# Revit family: HVAC-Fireplaces_Kalfire Fireplaces_e-one-130s-holographic-fireplace1
name_source: partatom
category: Specialty Equipment
units: mm (PartAtom-declared; Revit-internal decimal feet)

## family parameters
Cut with Voids When Loaded = No
Host = Face
OmniClass Number = 23.19.17.00
OmniClass Title = Fireplaces
Part Type = Normal
Room Calculation Point = No
Round Connector Dimension = Use Diameter
Shared = No

## types (1)
- E-one 130S Holographic Fireplace
    Area required = 1000 mm²
    Assembly Code = D3020.10
    Consumption (excl. Atmos Heating) = 110 W
    Consumption (incl. Atmos Heating) = 2 kW
    Date Updated = -
    Default Elevation = 1219 mm
    Description = The Kalfire E-one 130S is an electric holographic fireplace with glass on the front, both sides and optional heating. The projection of 3D holographic flames on the handmade logs imitates true-to-life fire. Options such as the realistic glow bed, crackling sound and optional Atmos Heating ensure an optimal fire experience.

A three-sided model is suitable as a see-through fireplace and takes your interior to the next level. Admire the holographic flames through the sides and be amazed by the realistic fire. At 130 cm wide, the E-one 130S is also perfectly used as a cinewall. Kalfire E-one holographic ambient fireplaces can be customised to suit personal preferences. Our exclusive and certified dealers are your helping hand in the installation and realisation of your dream design.

Atmos Heating: atmosphere fire with heat

The E-one is available with an innovative heating element called Atmos Heating. This element is exclusively available for the built-in versions of the Kalfire E-one (all variants except the E-one 100F FR). The heating element provides a pleasant and continuous flow of warm air at a 45-degree angle. This heating ensures an optimal fire experience that is unique for electric fireplaces.

Create your own fire

We give you options to create your own fire. Among other things, personalise the intensity and height of the flames, shuffle through flame images, choose the sound and intensity of the glow bed. Save all these settings in the Kalfire Moods, so that from now on you can watch your own fire at the click of a button.

The height of the E-one 130S ranges from 597 to 728.4 mm, depending on whether the atmos heating system is added
    Fire resistance of materials = All materials must withstand a temperture of minimum 80 degrees.
    Glass Material = Kalfire Fireplaces - Glass - Glass
    Installation instructions = https://www.dropbox.com
    Keynote = 15500
    Manufacturer = Kalfire Fireplaces
    Model = E-one 130S Holographic Fireplace
    Number of Poles = 3
    Power Factor = 0.8
    Product Documentation Link = https://www.dropbox.com
    Product Material = Kalfire Fireplaces - Metal - Iron
    Product Page URL = https://kalfire.com
    Product certification = https://www.dropbox.com
    Product data url = https://www.bimobject.com
    URL = https://kalfire.com
    Ventilation = Ventilation must be provided at both the bottom and top of the housing.
    Version = 1
    Voltage = 230 V

## geometry (parser evidence)
native form markers: Sweep x2
no freeform markers — native parametric forms only
